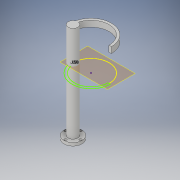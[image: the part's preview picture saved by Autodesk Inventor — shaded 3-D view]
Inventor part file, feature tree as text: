
AUTODESK INVENTOR PART (.ipt)
format: ipt  version: 2017 (Build 210142000, 142)  size: 146,944 bytes
history: native  units: in
note: dims shown in document units (in); Inventor stores cm internally (conversion verified against a paired STEP export)
features: sketch x5, extrude x3, hole x1, plane x1, projected_geometry x1
ambient origin geometry x8: Origin, YZ Plane, XZ Plane, XY Plane, X Axis, Y Axis, Z Axis, Center Point
bodies: Solid1 (feature_tree)
feature tree (11):
  extrude  "Extrusion1"  Depth=4.0in TaperAngle=0.0deg
  sketch  "Sketch2"  dims[d64=0.1in d65=0.1in]
  extrude  "Extrusion5"  Depth=0.1in
  extrude  "Extrusion6"  Depth=0.75in
  hole  "Hole1"  [1 undecoded]
  plane  "Work Plane6"
  sketch  "Sketch6"  dims[d70=0.25in d71=0.0in d72=0.75in d73=0.125in d74=0.0in d79=0.315in d80=0.315in d81=0.315in d82=0.315in d83=0.098in d84=0.75in d85=0.375in d86=0.25in d87=0.5635in d88=1.0in d89=0.8108in d90=-1.375in d91=0.05in d92=0.1in]
  sketch  "Sketch1"  dims[d0=0.4in d1=4.0in d2=0.0in]
  projected_geometry  "Projected Loop1"
  sketch  "Sketch4"  dims[d66=1.5in d67=0.75in]
  sketch  "Sketch5"  dims[d68=180.0deg d69=0.85in]
note: 1 required parameter value undecoded (feature->parameter linkage not recoverable at this tier; creation-order binding heuristic only, values carry confidence <= 0.55)
